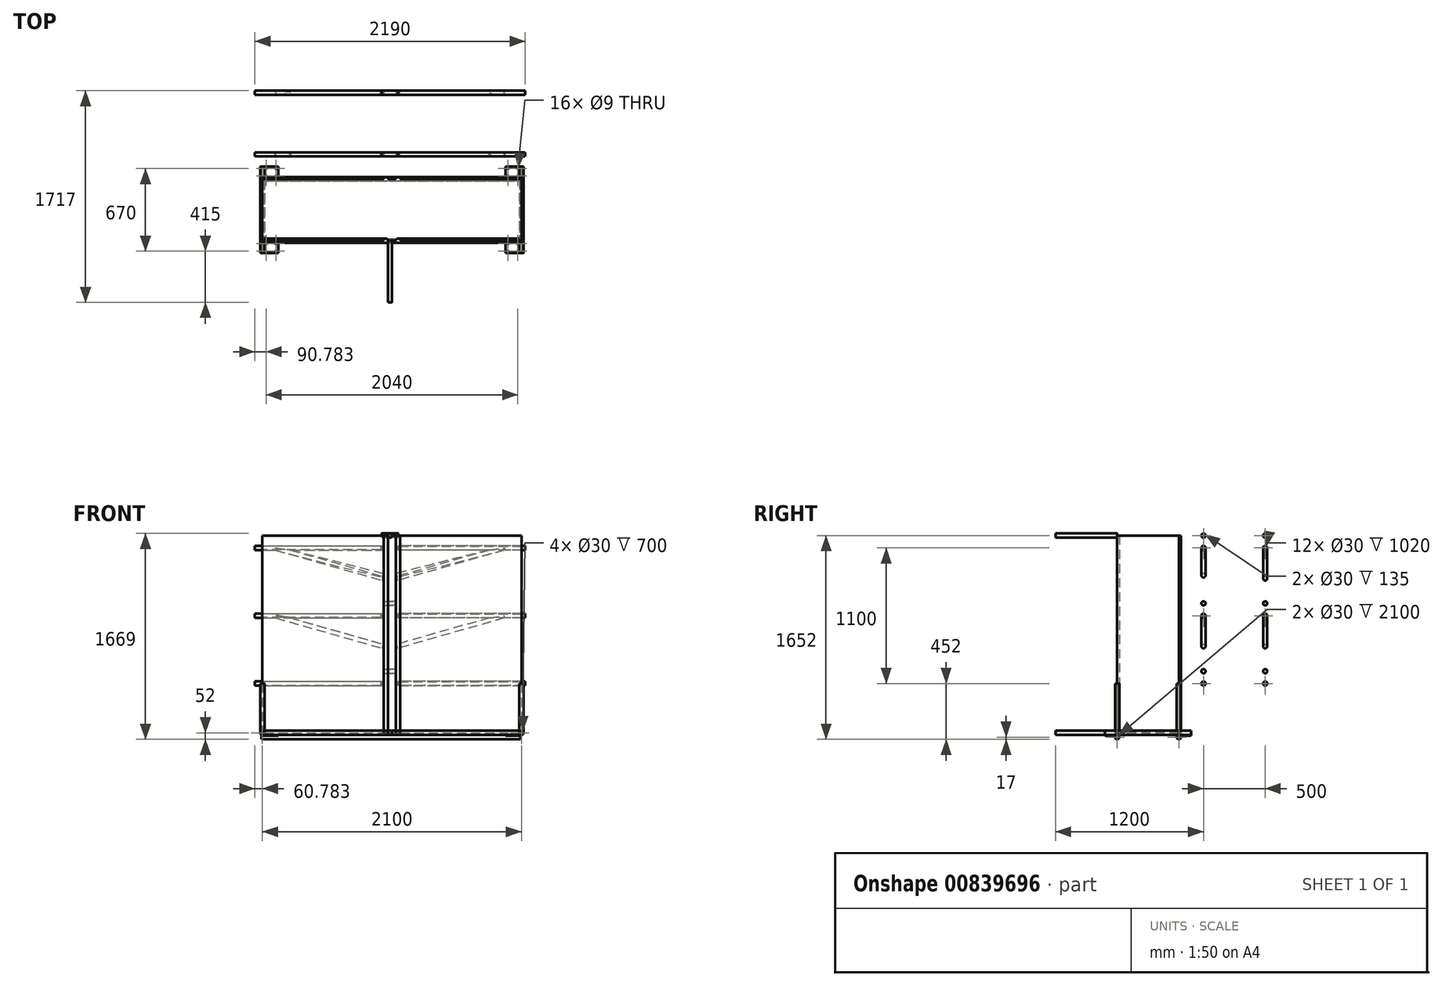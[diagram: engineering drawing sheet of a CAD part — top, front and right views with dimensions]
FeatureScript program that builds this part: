
annotation { "Feature Type Name" : "Feature", "Feature Type Description" : "" }
export const myFeature = defineFeature(function(context is Context, id is Id, definition is map)
    precondition{}
    {
        {
            var Q0;
            Q0=qCreatedBy(makeId("Top.planeOp"),FACE);
            var sketch = newSketch(context, id + "F0", { "sketchPlane" : qUnion([Q0])});
            skLineSegment(sketch, "E0.bottom", {"start": v(-1042.1, -100) * mm, "end": v(-59.1, -100) * mm});
            skLineSegment(sketch, "E0.top", {"start": v(-1042.1, -600) * mm, "end": v(-59.1, -600) * mm});
            skLineSegment(sketch, "E0.left", {"start": v(-1042.1, -100) * mm, "end": v(-1042.1, -600) * mm});
            skLineSegment(sketch, "E0.right", {"start": v(1057.9, -100) * mm, "end": v(1057.9, -600) * mm});
            skLineSegment(sketch, "E1", {"start": v(-1042.1, -100) * mm, "end": v(-1042.1, 0) * mm});
            skLineSegment(sketch, "E2", {"start": v(-1042.1, -600) * mm, "end": v(-1042.1, -700) * mm});
            skLineSegment(sketch, "E3", {"start": v(1057.9, -100) * mm, "end": v(1057.9, 0) * mm});
            skLineSegment(sketch, "E4", {"start": v(1057.9, -600) * mm, "end": v(1057.9, -700) * mm});
            skCircle(sketch, "E5", {"center": v(-42.1, -100) * mm, "radius": 17 * mm});
            skCircle(sketch, "E6", {"center": v(57.9, -100) * mm, "radius": 17 * mm});
            skLineSegment(sketch, "E7", {"start": v(1057.9, -350) * mm, "end": v(160.93, -350) * mm, "construction": true});
            skCircle(sketch, "E8.MirrorC", {"center": v(-42.1, -600) * mm, "radius": 17 * mm});
            skCircle(sketch, "E9.MirrorC", {"center": v(57.9, -600) * mm, "radius": 17 * mm});
            skLineSegment(sketch, "E10.trimOffspring", {"start": v(-25.1, -100) * mm, "end": v(40.9, -100) * mm});
            skLineSegment(sketch, "E11.trimOffspring", {"start": v(74.9, -100) * mm, "end": v(1057.9, -100) * mm});
            skLineSegment(sketch, "E12.trimOffspring", {"start": v(-25.1, -600) * mm, "end": v(40.9, -600) * mm});
            skLineSegment(sketch, "E13.trimOffspring", {"start": v(74.9, -600) * mm, "end": v(1057.9, -600) * mm});
            skSolve(sketch);
        }
        {
            var Q0;
            {var subQ0=sQuery(id+"F0.wireOp",EDGE,"E5");var subQ1=makeQuery(id+"F0.imprint","INTERSECT",VERTEX,{"derivedFrom":[sQuery(id+"F0.wireOp",EDGE,"E0.bottom"),subQ0]});Q0=makeQuery(id+"F0.imprint","IMPRINT",FACE,{"disambiguationData":[TD([[makeQuery(id+"F0.imprint","IMPRINT",EDGE,{"disambiguationData":[TD([[subQ1,1.0]])],"derivedFrom":subQ0}),1.0]])]});}
            var Q1;
            {var subQ0=sQuery(id+"F0.wireOp",EDGE,"E6");var subQ1=makeQuery(id+"F0.imprint","INTERSECT",VERTEX,{"derivedFrom":[subQ0,sQuery(id+"F0.wireOp",EDGE,"E10.trimOffspring")]});Q1=makeQuery(id+"F0.imprint","IMPRINT",FACE,{"disambiguationData":[TD([[makeQuery(id+"F0.imprint","IMPRINT",EDGE,{"disambiguationData":[TD([[subQ1,1.0]])],"derivedFrom":subQ0}),1.0]])]});}
            var Q2;
            {var subQ0=sQuery(id+"F0.wireOp",EDGE,"E8.MirrorC");var subQ1=makeQuery(id+"F0.imprint","INTERSECT",VERTEX,{"derivedFrom":[sQuery(id+"F0.wireOp",EDGE,"E0.top"),subQ0]});Q2=makeQuery(id+"F0.imprint","IMPRINT",FACE,{"disambiguationData":[TD([[makeQuery(id+"F0.imprint","IMPRINT",EDGE,{"disambiguationData":[TD([[subQ1,1.0]])],"derivedFrom":subQ0}),-1.0]])]});}
            var Q3;
            {var subQ0=sQuery(id+"F0.wireOp",EDGE,"E9.MirrorC");var subQ1=makeQuery(id+"F0.imprint","INTERSECT",VERTEX,{"derivedFrom":[subQ0,sQuery(id+"F0.wireOp",EDGE,"E12.trimOffspring")]});Q3=makeQuery(id+"F0.imprint","IMPRINT",FACE,{"disambiguationData":[TD([[makeQuery(id+"F0.imprint","IMPRINT",EDGE,{"disambiguationData":[TD([[subQ1,1.0]])],"derivedFrom":subQ0}),-1.0]])]});}
            extrude(context, id + "F1", {"entities" : qUnion([Q0, Q1, Q2, Q3]), "depth" : 1600 * mm, "offsetDistance" : 25 * mm});
        }
        {
            var Q0;
            Q0=sQuery(id+"F0.wireOp",EDGE,"E1");
            cPlane(context, id + "F2", {"entities" : qUnion([Q0]), "cplaneType" : CPlaneType.MID_PLANE, "offset" : 25 * mm, "width" : 150 * mm, "height" : 150 * mm});
        }
        {
            var Q0;
            Q0=qCreatedBy(id+"F2.planeOp",FACE);
            var sketch = newSketch(context, id + "F3", { "sketchPlane" : qUnion([Q0])});
            skCircle(sketch, "E14", {"center": v(1042.1, 0) * mm, "radius": 17 * mm});
            skCircle(sketch, "E15", {"center": v(-1057.9, 0) * mm, "radius": 17 * mm});
            skSolve(sketch);
        }
        {
            var Q0;
            Q0 = qSketchRegion(id + "F3", true);
            extrude(context, id + "F4", {"entities" : qUnion([Q0]), "depth" : 50 * mm, "offsetDistance" : 25 * mm, "hasSecondDirection" : true, "secondDirectionOppositeDirection" : true, "secondDirectionDepth" : 650 * mm});
        }
        {
            var Q0;
            Q0 = qSketchRegion(id + "F3", true);
            extrude(context, id + "F5", {"entities" : qUnion([Q0]), "depth" : 50 * mm, "offsetDistance" : 25 * mm, "hasSecondDirection" : true, "secondDirectionOppositeDirection" : true, "secondDirectionDepth" : 650 * mm});
        }
        {
            var Q0;
            Q0=sQuery(id+"F0.wireOp",EDGE,"E0.bottom");
            cPlane(context, id + "F6", {"entities" : qUnion([Q0]), "cplaneType" : CPlaneType.MID_PLANE, "offset" : 25 * mm, "width" : 150 * mm, "height" : 150 * mm});
        }
        {
            var Q0;
            Q0=qCreatedBy(id+"F6.planeOp",FACE);
            var sketch = newSketch(context, id + "F7", { "sketchPlane" : qUnion([Q0])});
            skCircle(sketch, "E16", {"center": v(-100, 0) * mm, "radius": 17 * mm});
            skCircle(sketch, "E17", {"center": v(-600, 0) * mm, "radius": 17 * mm});
            skSolve(sketch);
        }
        {
            var Q0;
            Q0 = qSketchRegion(id + "F7", true);
            extrude(context, id + "F8", {"entities" : qUnion([Q0]), "oppositeDirection" : true, "depth" : 500 * mm, "offsetDistance" : 25 * mm, "hasSecondDirection" : true, "secondDirectionOppositeDirection" : false, "secondDirectionDepth" : 1600 * mm});
        }
        {
            var Q0;
            Q0=qCreatedBy(makeId("Top.planeOp"),FACE);
            cPlane(context, id + "F9", {"entities" : qUnion([Q0]), "cplaneType" : CPlaneType.OFFSET, "offset" : 17.5 * mm, "oppositeDirection" : true, "width" : 150 * mm, "height" : 150 * mm});
        }
        {
            var Q0;
            Q0=qCreatedBy(id+"F9.planeOp",FACE);
            var sketch = newSketch(context, id + "F10", { "sketchPlane" : qUnion([Q0])});
            skLineSegment(sketch, "E18.bottom", {"start": v(-1042.1, -600) * mm, "end": v(-912.1, -600) * mm});
            skLineSegment(sketch, "E18.top", {"start": v(-1042.1, -700) * mm, "end": v(-912.1, -700) * mm});
            skLineSegment(sketch, "E18.left", {"start": v(-1042.1, -600) * mm, "end": v(-1042.1, -700) * mm});
            skLineSegment(sketch, "E18.right", {"start": v(-912.1, -600) * mm, "end": v(-912.1, -700) * mm});
            skCircle(sketch, "E19", {"center": v(-1012.1, -685) * mm, "radius": 4.5 * mm});
            skCircle(sketch, "E20", {"center": v(-932.1, -685) * mm, "radius": 4.5 * mm});
            skCircle(sketch, "E21", {"center": v(-1012.1, -625) * mm, "radius": 4.5 * mm});
            skCircle(sketch, "E22", {"center": v(-932.1, -625) * mm, "radius": 4.5 * mm});
            skLineSegment(sketch, "E23.bottom", {"start": v(-1007.6, -685) * mm, "end": v(-936.6, -685) * mm, "construction": true});
            skLineSegment(sketch, "E23.top", {"start": v(-1007.6, -625) * mm, "end": v(-936.6, -625) * mm, "construction": true});
            skLineSegment(sketch, "E23.left", {"start": v(-1012.1, -680.5) * mm, "end": v(-1012.1, -629.5) * mm, "construction": true});
            skLineSegment(sketch, "E23.right", {"start": v(-932.1, -680.5) * mm, "end": v(-932.1, -629.5) * mm, "construction": true});
            skLineSegment(sketch, "E24", {"start": v(-972.1, -685) * mm, "end": v(-972.1, -625) * mm, "construction": true});
            skLineSegment(sketch, "E25", {"start": v(-1012.1, -655) * mm, "end": v(-932.1, -655) * mm, "construction": true});
            skLineSegment(sketch, "E26", {"start": v(7.9, -600) * mm, "end": v(7.9, -303.37) * mm, "construction": true});
            skLineSegment(sketch, "E27", {"start": v(-1042.1, -350) * mm, "end": v(-775.86, -350) * mm, "construction": true});
            skLineSegment(sketch, "E28.MirrorCS", {"start": v(-1042.1, -100) * mm, "end": v(-912.1, -100) * mm});
            skLineSegment(sketch, "E29.MirrorCS", {"start": v(-912.1, -100) * mm, "end": v(-912.1, 0) * mm});
            skLineSegment(sketch, "E30.MirrorCS", {"start": v(-1042.1, 0) * mm, "end": v(-912.1, 0) * mm});
            skLineSegment(sketch, "E31.MirrorCS", {"start": v(-1042.1, -100) * mm, "end": v(-1042.1, 0) * mm});
            skCircle(sketch, "E32.MirrorC", {"center": v(-1012.1, -15) * mm, "radius": 4.5 * mm});
            skCircle(sketch, "E33.MirrorC", {"center": v(-932.1, -15) * mm, "radius": 4.5 * mm});
            skCircle(sketch, "E34.MirrorC", {"center": v(-932.1, -75) * mm, "radius": 4.5 * mm});
            skCircle(sketch, "E35.MirrorC", {"center": v(-1012.1, -75) * mm, "radius": 4.5 * mm});
            skLineSegment(sketch, "E36.MirrorCS", {"start": v(1057.9, -700) * mm, "end": v(927.9, -700) * mm});
            skLineSegment(sketch, "E37.MirrorCS", {"start": v(1057.9, -600) * mm, "end": v(1057.9, -700) * mm});
            skLineSegment(sketch, "E38.MirrorCS", {"start": v(927.9, -600) * mm, "end": v(927.9, -700) * mm});
            skLineSegment(sketch, "E39.MirrorCS", {"start": v(1057.9, -600) * mm, "end": v(927.9, -600) * mm});
            skCircle(sketch, "E40.MirrorC", {"center": v(947.9, -625) * mm, "radius": 4.5 * mm});
            skCircle(sketch, "E41.MirrorC", {"center": v(947.9, -685) * mm, "radius": 4.5 * mm});
            skCircle(sketch, "E42.MirrorC", {"center": v(1027.9, -685) * mm, "radius": 4.5 * mm});
            skCircle(sketch, "E43.MirrorC", {"center": v(1027.9, -625) * mm, "radius": 4.5 * mm});
            skLineSegment(sketch, "E44.MirrorCS", {"start": v(1057.9, -100) * mm, "end": v(927.9, -100) * mm});
            skLineSegment(sketch, "E45.MirrorCS", {"start": v(927.9, -100) * mm, "end": v(927.9, 0) * mm});
            skLineSegment(sketch, "E46.MirrorCS", {"start": v(1057.9, -100) * mm, "end": v(1057.9, 0) * mm});
            skLineSegment(sketch, "E47.MirrorCS", {"start": v(1057.9, 0) * mm, "end": v(927.9, 0) * mm});
            skCircle(sketch, "E48.MirrorC", {"center": v(947.9, -15) * mm, "radius": 4.5 * mm});
            skCircle(sketch, "E49.MirrorC", {"center": v(947.9, -75) * mm, "radius": 4.5 * mm});
            skCircle(sketch, "E50.MirrorC", {"center": v(1027.9, -75) * mm, "radius": 4.5 * mm});
            skCircle(sketch, "E51.MirrorC", {"center": v(1027.9, -15) * mm, "radius": 4.5 * mm});
            skLineSegment(sketch, "E52", {"start": v(-972.1, -700) * mm, "end": v(-972.1, -600) * mm, "construction": true});
            skLineSegment(sketch, "E53", {"start": v(-1042.1, -655) * mm, "end": v(-912.1, -655) * mm, "construction": true});
            skSolve(sketch);
        }
        {
            var Q0;
            Q0 = qSketchRegion(id + "F10", true);
            extrude(context, id + "F11", {"entities" : qUnion([Q0]), "oppositeDirection" : true, "depth" : 4 * mm, "offsetDistance" : 25 * mm});
        }
        {
            var Q0;
            Q0=qCreatedBy(id+"F9.planeOp",FACE);
            cPlane(context, id + "F12", {"entities" : qUnion([Q0]), "cplaneType" : CPlaneType.OFFSET, "offset" : 17.5 * mm, "oppositeDirection" : true, "width" : 150 * mm, "height" : 150 * mm});
        }
        {
            var Q0;
            Q0=qCreatedBy(id+"F12.planeOp",FACE);
            var sketch = newSketch(context, id + "F13", { "sketchPlane" : qUnion([Q0])});
            skLineSegment(sketch, "E54", {"start": v(-1042.1, -600) * mm, "end": v(1057.9, -600) * mm});
            skLineSegment(sketch, "E55", {"start": v(-1042.1, -100) * mm, "end": v(1057.9, -100) * mm});
            skSolve(sketch);
        }
        {
            var Q0;
            Q0=qCreatedBy(id+"F6.planeOp",FACE);
            var sketch = newSketch(context, id + "F14", { "sketchPlane" : qUnion([Q0])});
            skCircle(sketch, "E56", {"center": v(-100, -35) * mm, "radius": 17 * mm});
            skCircle(sketch, "E57", {"center": v(-600, -35) * mm, "radius": 17 * mm});
            skSolve(sketch);
        }
        {
            var Q0;
            Q0 = qSketchRegion(id + "F14", true);
            extrude(context, id + "F15", {"entities" : qUnion([Q0]), "oppositeDirection" : true, "depth" : 500 * mm, "offsetDistance" : 25 * mm, "hasSecondDirection" : true, "secondDirectionOppositeDirection" : false, "secondDirectionDepth" : 1600 * mm});
        }
        {
            var Q0;
            Q0=makeQuery(id+"F1.opExtrude","SWEPT_FACE",FACE,{"disambiguationData":[OSD([sQuery(id+"F0.wireOp",EDGE,"E9.MirrorC")])]});
            var Q1;
            Q1=makeQuery(id+"F1.opExtrude","SWEPT_FACE",FACE,{"disambiguationData":[OSD([sQuery(id+"F0.wireOp",EDGE,"E8.MirrorC")])]});
            cPlane(context, id + "F16", {"entities" : qUnion([Q0, Q1]), "cplaneType" : CPlaneType.LINE_ANGLE, "offset" : 25 * mm, "angle" : 0 * degree, "width" : 150 * mm, "height" : 150 * mm});
        }
        {
            var Q0;
            Q0=qCreatedBy(id+"F16.planeOp",FACE);
            var sketch = newSketch(context, id + "F17", { "sketchPlane" : qUnion([Q0])});
            skCircle(sketch, "E58", {"center": v(-7.9, 0) * mm, "radius": 17 * mm});
            skSolve(sketch);
        }
        {
            var Q0;
            Q0 = qSketchRegion(id + "F17", true);
            extrude(context, id + "F18", {"entities" : qUnion([Q0]), "depth" : 500 * mm, "offsetDistance" : 25 * mm});
        }
        {
            var Q0;
            Q0=qCreatedBy(id+"F16.planeOp",FACE);
            var sketch = newSketch(context, id + "F19", { "sketchPlane" : qUnion([Q0])});
            skLineSegment(sketch, "E59", {"start": v(-57.9, 0) * mm, "end": v(-57.9, 1600) * mm});
            skLineSegment(sketch, "E60", {"start": v(42.1, 0) * mm, "end": v(42.1, 1600) * mm});
            skLineSegment(sketch, "E61", {"start": v(42.1, 500) * mm, "end": v(-57.9, 500) * mm});
            skLineSegment(sketch, "E62", {"start": v(42.1, 1050) * mm, "end": v(-57.9, 1050) * mm});
            skLineSegment(sketch, "E63", {"start": v(-57.9, 400) * mm, "end": v(-1087.9, 400) * mm});
            skLineSegment(sketch, "E64", {"start": v(42.1, 400) * mm, "end": v(1072.1, 400) * mm});
            skLineSegment(sketch, "E65", {"start": v(-57.9, 950) * mm, "end": v(-1087.9, 950) * mm});
            skLineSegment(sketch, "E66", {"start": v(42.1, 950) * mm, "end": v(1072.1, 950) * mm});
            skLineSegment(sketch, "E67", {"start": v(-57.9, 1500) * mm, "end": v(-1087.9, 1500) * mm});
            skLineSegment(sketch, "E68", {"start": v(42.1, 1500) * mm, "end": v(1072.1, 1500) * mm});
            skLineSegment(sketch, "E69", {"start": v(42.1, 1600) * mm, "end": v(-57.9, 1600) * mm});
            skLineSegment(sketch, "E70", {"start": v(-1057.9, 400) * mm, "end": v(-1057.9, 0) * mm});
            skLineSegment(sketch, "E71", {"start": v(1042.1, 400) * mm, "end": v(1042.1, 0) * mm});
            skLineSegment(sketch, "E72", {"start": v(-57.9, 700) * mm, "end": v(-937.9, 950) * mm});
            skLineSegment(sketch, "E73", {"start": v(42.1, 700) * mm, "end": v(922.1, 950) * mm});
            skLineSegment(sketch, "E74", {"start": v(-57.9, 1250) * mm, "end": v(-937.9, 1500) * mm});
            skLineSegment(sketch, "E75", {"start": v(42.1, 1250) * mm, "end": v(922.1, 1500) * mm});
            skSolve(sketch);
        }
        {
            var Q0;
            Q0=sQuery(id+"F19.wireOp",EDGE,"E67");
            cPlane(context, id + "F20", {"entities" : qUnion([Q0]), "cplaneType" : CPlaneType.MID_PLANE, "offset" : 25 * mm, "width" : 150 * mm, "height" : 150 * mm});
        }
        {
            var Q0;
            Q0=qCreatedBy(id+"F20.planeOp",FACE);
            var sketch = newSketch(context, id + "F21", { "sketchPlane" : qUnion([Q0])});
            skCircle(sketch, "E76", {"center": v(-600, 1500) * mm, "radius": 17 * mm});
            skCircle(sketch, "E77", {"center": v(-600, 950) * mm, "radius": 17 * mm});
            skCircle(sketch, "E78", {"center": v(-600, 400) * mm, "radius": 17 * mm});
            skSolve(sketch);
        }
        {
            var Q0;
            Q0 = qSketchRegion(id + "F21", true);
            extrude(context, id + "F22", {"entities" : qUnion([Q0]), "operationType" : NewBodyOperationType.ADD, "depth" : 530 * mm, "offsetDistance" : 25 * mm, "hasSecondDirection" : true, "secondDirectionOppositeDirection" : true, "secondDirectionDepth" : 500 * mm});
        }
        {
            var Q0;
            Q0=sQuery(id+"F19.wireOp",EDGE,"E68");
            cPlane(context, id + "F23", {"entities" : qUnion([Q0]), "cplaneType" : CPlaneType.MID_PLANE, "offset" : 25 * mm, "width" : 150 * mm, "height" : 150 * mm});
        }
        {
            var Q0;
            Q0=qCreatedBy(id+"F23.planeOp",FACE);
            var sketch = newSketch(context, id + "F24", { "sketchPlane" : qUnion([Q0])});
            skCircle(sketch, "E79", {"center": v(600, 1500) * mm, "radius": 17 * mm});
            skCircle(sketch, "E80", {"center": v(600, 950) * mm, "radius": 17 * mm});
            skCircle(sketch, "E81", {"center": v(600, 400) * mm, "radius": 17 * mm});
            skSolve(sketch);
        }
        {
            var Q0;
            Q0 = qSketchRegion(id + "F24", true);
            extrude(context, id + "F25", {"entities" : qUnion([Q0]), "operationType" : NewBodyOperationType.ADD, "depth" : 530 * mm, "offsetDistance" : 25 * mm, "hasSecondDirection" : true, "secondDirectionOppositeDirection" : true, "secondDirectionDepth" : 500 * mm});
        }
        {
            var Q0;
            Q0=sQuery(id+"F19.wireOp",EDGE,"E74");
            cPlane(context, id + "F26", {"entities" : qUnion([Q0]), "cplaneType" : CPlaneType.MID_PLANE, "offset" : 25 * mm, "width" : 150 * mm, "height" : 150 * mm});
        }
        {
            var Q0;
            Q0=qCreatedBy(id+"F26.planeOp",FACE);
            var sketch = newSketch(context, id + "F27", { "sketchPlane" : qUnion([Q0])});
            skCircle(sketch, "E82", {"center": v(-600, 1186.6) * mm, "radius": 17 * mm});
            skSolve(sketch);
        }
        {
            var Q0;
            Q0 = qSketchRegion(id + "F27", true);
            extrude(context, id + "F28", {"entities" : qUnion([Q0]), "operationType" : NewBodyOperationType.ADD, "depth" : 450 * mm, "offsetDistance" : 25 * mm, "hasSecondDirection" : true, "secondDirectionOppositeDirection" : true, "secondDirectionDepth" : 450 * mm});
        }
        {
            var Q0;
            Q0=sQuery(id+"F19.wireOp",EDGE,"E75");
            cPlane(context, id + "F29", {"entities" : qUnion([Q0]), "cplaneType" : CPlaneType.MID_PLANE, "offset" : 25 * mm, "width" : 150 * mm, "height" : 150 * mm});
        }
        {
            var Q0;
            Q0=qCreatedBy(id+"F29.planeOp",FACE);
            var sketch = newSketch(context, id + "F30", { "sketchPlane" : qUnion([Q0])});
            skCircle(sketch, "E83", {"center": v(600, 1190.91) * mm, "radius": 17 * mm});
            skSolve(sketch);
        }
        {
            var Q0;
            Q0 = qSketchRegion(id + "F30", true);
            extrude(context, id + "F31", {"entities" : qUnion([Q0]), "operationType" : NewBodyOperationType.ADD, "depth" : 450 * mm, "offsetDistance" : 25 * mm, "hasSecondDirection" : true, "secondDirectionOppositeDirection" : true, "secondDirectionDepth" : 450 * mm});
        }
        {
            var Q0;
            Q0=sQuery(id+"F19.wireOp",EDGE,"E69");
            cPlane(context, id + "F32", {"entities" : qUnion([Q0]), "cplaneType" : CPlaneType.MID_PLANE, "offset" : 25 * mm, "width" : 150 * mm, "height" : 150 * mm});
        }
        {
            var Q0;
            Q0=qCreatedBy(id+"F32.planeOp",FACE);
            var sketch = newSketch(context, id + "F33", { "sketchPlane" : qUnion([Q0])});
            skCircle(sketch, "E84", {"center": v(-600, 1600) * mm, "radius": 17 * mm});
            skCircle(sketch, "E85", {"center": v(-600, 1050) * mm, "radius": 17 * mm});
            skCircle(sketch, "E86", {"center": v(-600, 500) * mm, "radius": 17 * mm});
            skSolve(sketch);
        }
        {
            var Q0;
            Q0=makeQuery(id+"F33.imprint","IMPRINT",FACE,{"disambiguationData":[TD([[makeQuery(id+"F33.imprint","IMPRINT",EDGE,{"derivedFrom":sQuery(id+"F33.wireOp",EDGE,"E85")}),1.0]])]});
            var Q1;
            Q1=makeQuery(id+"F33.imprint","IMPRINT",FACE,{"disambiguationData":[TD([[makeQuery(id+"F33.imprint","IMPRINT",EDGE,{"derivedFrom":sQuery(id+"F33.wireOp",EDGE,"E86")}),1.0]])]});
            extrude(context, id + "F34", {"entities" : qUnion([Q0, Q1]), "depth" : 50 * mm, "offsetDistance" : 25 * mm, "hasSecondDirection" : true, "secondDirectionOppositeDirection" : true, "secondDirectionDepth" : 50 * mm});
        }
        {
            var Q0;
            Q0=makeQuery(id+"F33.imprint","IMPRINT",FACE,{"disambiguationData":[TD([[makeQuery(id+"F33.imprint","IMPRINT",EDGE,{"derivedFrom":sQuery(id+"F33.wireOp",EDGE,"E84")}),1.0]])]});
            extrude(context, id + "F35", {"entities" : qUnion([Q0]), "depth" : 67.5 * mm, "offsetDistance" : 25 * mm, "hasSecondDirection" : true, "secondDirectionOppositeDirection" : true, "secondDirectionDepth" : 67.5 * mm});
        }
        {
            var Q0;
            Q0=sQuery(id+"F19.wireOp",EDGE,"E72");
            cPlane(context, id + "F36", {"entities" : qUnion([Q0]), "cplaneType" : CPlaneType.MID_PLANE, "offset" : 25 * mm, "width" : 150 * mm, "height" : 150 * mm});
        }
        {
            var Q0;
            Q0=qCreatedBy(id+"F36.planeOp",FACE);
            var sketch = newSketch(context, id + "F37", { "sketchPlane" : qUnion([Q0])});
            skCircle(sketch, "E87", {"center": v(-600, 657.53) * mm, "radius": 17 * mm});
            skSolve(sketch);
        }
        {
            var Q0;
            Q0 = qSketchRegion(id + "F37", true);
            extrude(context, id + "F38", {"entities" : qUnion([Q0]), "depth" : 450 * mm, "offsetDistance" : 25 * mm, "hasSecondDirection" : true, "secondDirectionOppositeDirection" : true, "secondDirectionDepth" : 450 * mm});
        }
        {
            var Q0;
            Q0=sQuery(id+"F19.wireOp",EDGE,"E73");
            cPlane(context, id + "F39", {"entities" : qUnion([Q0]), "cplaneType" : CPlaneType.MID_PLANE, "offset" : 25 * mm, "width" : 150 * mm, "height" : 150 * mm});
        }
        {
            var Q0;
            Q0=qCreatedBy(id+"F39.planeOp",FACE);
            var sketch = newSketch(context, id + "F40", { "sketchPlane" : qUnion([Q0])});
            skCircle(sketch, "E88", {"center": v(600, 661.85) * mm, "radius": 17 * mm});
            skSolve(sketch);
        }
        {
            var Q0;
            Q0 = qSketchRegion(id + "F40", true);
            extrude(context, id + "F41", {"entities" : qUnion([Q0]), "operationType" : NewBodyOperationType.ADD, "depth" : 450 * mm, "offsetDistance" : 25 * mm, "hasSecondDirection" : true, "secondDirectionOppositeDirection" : true, "secondDirectionDepth" : 450 * mm});
        }
        {
            var Q0;
            Q0=qCreatedBy(id+"F16.planeOp",FACE);
            cPlane(context, id + "F42", {"entities" : qUnion([Q0]), "cplaneType" : CPlaneType.OFFSET, "offset" : 500 * mm, "width" : 150 * mm, "height" : 150 * mm});
        }
        {
            var Q0;
            Q0=qCreatedBy(id+"F42.planeOp",FACE);
            var sketch = newSketch(context, id + "F43", { "sketchPlane" : qUnion([Q0])});
            skLineSegment(sketch, "E89", {"start": v(42.1, 0) * mm, "end": v(42.1, 1600) * mm});
            skLineSegment(sketch, "E90", {"start": v(-57.9, 0) * mm, "end": v(-57.9, 1600) * mm});
            skLineSegment(sketch, "E91", {"start": v(-57.9, 500) * mm, "end": v(42.1, 500) * mm});
            skLineSegment(sketch, "E92", {"start": v(-57.9, 1050) * mm, "end": v(42.1, 1050) * mm});
            skLineSegment(sketch, "E93", {"start": v(-57.9, 1600) * mm, "end": v(42.1, 1600) * mm});
            skLineSegment(sketch, "E94", {"start": v(42.1, 400) * mm, "end": v(1072.1, 400) * mm});
            skLineSegment(sketch, "E95", {"start": v(-57.9, 400) * mm, "end": v(-1087.9, 400) * mm});
            skLineSegment(sketch, "E96", {"start": v(42.1, 950) * mm, "end": v(1072.1, 950) * mm});
            skLineSegment(sketch, "E97", {"start": v(-57.9, 950) * mm, "end": v(-1087.9, 950) * mm});
            skLineSegment(sketch, "E98", {"start": v(42.1, 1500) * mm, "end": v(1072.1, 1500) * mm});
            skLineSegment(sketch, "E99", {"start": v(-57.9, 1500) * mm, "end": v(-1087.9, 1500) * mm});
            skLineSegment(sketch, "E100", {"start": v(1042.1, 400) * mm, "end": v(1042.1, 0) * mm});
            skLineSegment(sketch, "E101", {"start": v(-1057.9, 400) * mm, "end": v(-1057.9, 0) * mm});
            skLineSegment(sketch, "E102", {"start": v(42.1, 700) * mm, "end": v(922.1, 950) * mm});
            skLineSegment(sketch, "E103", {"start": v(42.1, 1274.83) * mm, "end": v(928.79, 1500) * mm});
            skLineSegment(sketch, "E104", {"start": v(-57.9, 1274.83) * mm, "end": v(-944.57, 1500) * mm});
            skLineSegment(sketch, "E105", {"start": v(-57.9, 700) * mm, "end": v(-937.9, 950) * mm});
            skSolve(sketch);
        }
        {
            var Q0;
            Q0=sQuery(id+"F43.wireOp",EDGE,"E98");
            cPlane(context, id + "F44", {"entities" : qUnion([Q0]), "cplaneType" : CPlaneType.MID_PLANE, "offset" : 25 * mm, "width" : 150 * mm, "height" : 150 * mm});
        }
        {
            var Q0;
            Q0=qCreatedBy(id+"F44.planeOp",FACE);
            var sketch = newSketch(context, id + "F45", { "sketchPlane" : qUnion([Q0])});
            skCircle(sketch, "E106", {"center": v(100, 1500) * mm, "radius": 17 * mm});
            skCircle(sketch, "E107", {"center": v(100, 950) * mm, "radius": 17 * mm});
            skCircle(sketch, "E108", {"center": v(100, 400) * mm, "radius": 17 * mm});
            skSolve(sketch);
        }
        {
            var Q0;
            Q0 = qSketchRegion(id + "F45", true);
            extrude(context, id + "F46", {"entities" : qUnion([Q0]), "operationType" : NewBodyOperationType.ADD, "depth" : 530 * mm, "offsetDistance" : 25 * mm, "hasSecondDirection" : true, "secondDirectionOppositeDirection" : true, "secondDirectionDepth" : 500 * mm});
        }
        {
            var Q0;
            Q0=sQuery(id+"F43.wireOp",EDGE,"E99");
            cPlane(context, id + "F47", {"entities" : qUnion([Q0]), "cplaneType" : CPlaneType.MID_PLANE, "offset" : 25 * mm, "width" : 150 * mm, "height" : 150 * mm});
        }
        {
            var Q0;
            Q0=qCreatedBy(id+"F47.planeOp",FACE);
            var sketch = newSketch(context, id + "F48", { "sketchPlane" : qUnion([Q0])});
            skCircle(sketch, "E109", {"center": v(-100, 1500) * mm, "radius": 17 * mm});
            skCircle(sketch, "E110", {"center": v(-100, 950) * mm, "radius": 17 * mm});
            skCircle(sketch, "E111", {"center": v(-100, 400) * mm, "radius": 17 * mm});
            skSolve(sketch);
        }
        {
            var Q0;
            Q0 = qSketchRegion(id + "F48", true);
            extrude(context, id + "F49", {"entities" : qUnion([Q0]), "operationType" : NewBodyOperationType.ADD, "depth" : 530 * mm, "offsetDistance" : 25 * mm, "hasSecondDirection" : true, "secondDirectionOppositeDirection" : true, "secondDirectionDepth" : 500 * mm});
        }
        {
            var Q0;
            Q0=sQuery(id+"F43.wireOp",EDGE,"E102");
            cPlane(context, id + "F50", {"entities" : qUnion([Q0]), "cplaneType" : CPlaneType.MID_PLANE, "offset" : 25 * mm, "width" : 150 * mm, "height" : 150 * mm});
        }
        {
            var Q0;
            Q0=qCreatedBy(id+"F50.planeOp",FACE);
            var sketch = newSketch(context, id + "F51", { "sketchPlane" : qUnion([Q0])});
            skCircle(sketch, "E112", {"center": v(100, 661.85) * mm, "radius": 17 * mm});
            skSolve(sketch);
        }
        {
            var Q0;
            Q0 = qSketchRegion(id + "F51", true);
            extrude(context, id + "F52", {"entities" : qUnion([Q0]), "operationType" : NewBodyOperationType.ADD, "depth" : 450 * mm, "offsetDistance" : 25 * mm, "hasSecondDirection" : true, "secondDirectionOppositeDirection" : true, "secondDirectionDepth" : 450 * mm});
        }
        {
            var Q0;
            Q0=sQuery(id+"F43.wireOp",EDGE,"E105");
            cPlane(context, id + "F53", {"entities" : qUnion([Q0]), "cplaneType" : CPlaneType.MID_PLANE, "offset" : 25 * mm, "width" : 150 * mm, "height" : 150 * mm});
        }
        {
            var Q0;
            Q0=qCreatedBy(id+"F53.planeOp",FACE);
            var sketch = newSketch(context, id + "F54", { "sketchPlane" : qUnion([Q0])});
            skCircle(sketch, "E113", {"center": v(-100, 657.53) * mm, "radius": 17 * mm});
            skSolve(sketch);
        }
        {
            var Q0;
            Q0 = qSketchRegion(id + "F54", true);
            extrude(context, id + "F55", {"entities" : qUnion([Q0]), "operationType" : NewBodyOperationType.ADD, "depth" : 450 * mm, "offsetDistance" : 25 * mm, "hasSecondDirection" : true, "secondDirectionOppositeDirection" : true, "secondDirectionDepth" : 450 * mm});
        }
        {
            var Q0;
            Q0=sQuery(id+"F43.wireOp",EDGE,"E92");
            cPlane(context, id + "F56", {"entities" : qUnion([Q0]), "cplaneType" : CPlaneType.MID_PLANE, "offset" : 25 * mm, "width" : 150 * mm, "height" : 150 * mm});
        }
        {
            var Q0;
            Q0=qCreatedBy(id+"F56.planeOp",FACE);
            var sketch = newSketch(context, id + "F57", { "sketchPlane" : qUnion([Q0])});
            skCircle(sketch, "E114", {"center": v(100, 1050) * mm, "radius": 17 * mm});
            skCircle(sketch, "E115", {"center": v(100, 500) * mm, "radius": 17 * mm});
            skCircle(sketch, "E116", {"center": v(100, 1600) * mm, "radius": 17 * mm});
            skSolve(sketch);
        }
        {
            var Q0;
            Q0=makeQuery(id+"F57.imprint","IMPRINT",FACE,{"disambiguationData":[TD([[makeQuery(id+"F57.imprint","IMPRINT",EDGE,{"derivedFrom":sQuery(id+"F57.wireOp",EDGE,"E114")}),1.0]])]});
            var Q1;
            Q1=makeQuery(id+"F57.imprint","IMPRINT",FACE,{"disambiguationData":[TD([[makeQuery(id+"F57.imprint","IMPRINT",EDGE,{"derivedFrom":sQuery(id+"F57.wireOp",EDGE,"E115")}),1.0]])]});
            extrude(context, id + "F58", {"entities" : qUnion([Q0, Q1]), "operationType" : NewBodyOperationType.ADD, "depth" : 50 * mm, "offsetDistance" : 25 * mm, "hasSecondDirection" : true, "secondDirectionOppositeDirection" : true, "secondDirectionDepth" : 50 * mm});
        }
        {
            var Q0;
            Q0=makeQuery(id+"F57.imprint","IMPRINT",FACE,{"disambiguationData":[TD([[makeQuery(id+"F57.imprint","IMPRINT",EDGE,{"derivedFrom":sQuery(id+"F57.wireOp",EDGE,"E116")}),1.0]])]});
            extrude(context, id + "F59", {"entities" : qUnion([Q0]), "depth" : 67.5 * mm, "offsetDistance" : 25 * mm, "hasSecondDirection" : true, "secondDirectionOppositeDirection" : true, "secondDirectionDepth" : 67.5 * mm});
        }
        {
            var Q0;
            Q0=sQuery(id+"F43.wireOp",EDGE,"E103");
            cPlane(context, id + "F60", {"entities" : qUnion([Q0]), "cplaneType" : CPlaneType.MID_PLANE, "offset" : 25 * mm, "width" : 150 * mm, "height" : 150 * mm});
        }
        {
            var Q0;
            Q0=qCreatedBy(id+"F60.planeOp",FACE);
            var sketch = newSketch(context, id + "F61", { "sketchPlane" : qUnion([Q0])});
            skCircle(sketch, "E117", {"center": v(100, 1225.25) * mm, "radius": 17 * mm});
            skSolve(sketch);
        }
        {
            var Q0;
            Q0 = qSketchRegion(id + "F61", true);
            extrude(context, id + "F62", {"entities" : qUnion([Q0]), "operationType" : NewBodyOperationType.ADD, "depth" : 450 * mm, "offsetDistance" : 25 * mm, "hasSecondDirection" : true, "secondDirectionOppositeDirection" : true, "secondDirectionDepth" : 450 * mm});
        }
        {
            var Q0;
            Q0=sQuery(id+"F43.wireOp",EDGE,"E104");
            cPlane(context, id + "F63", {"entities" : qUnion([Q0]), "cplaneType" : CPlaneType.MID_PLANE, "offset" : 25 * mm, "width" : 150 * mm, "height" : 150 * mm});
        }
        {
            var Q0;
            Q0=qCreatedBy(id+"F63.planeOp",FACE);
            var sketch = newSketch(context, id + "F64", { "sketchPlane" : qUnion([Q0])});
            skCircle(sketch, "E118", {"center": v(-100, 1221.36) * mm, "radius": 17 * mm});
            skSolve(sketch);
        }
        {
            var Q0;
            Q0 = qSketchRegion(id + "F64", true);
            extrude(context, id + "F65", {"entities" : qUnion([Q0]), "operationType" : NewBodyOperationType.ADD, "depth" : 450 * mm, "offsetDistance" : 25 * mm, "hasSecondDirection" : true, "secondDirectionOppositeDirection" : true, "secondDirectionDepth" : 450 * mm});
        }
        {
            var Q0;
            Q0=sQuery(id+"F19.wireOp",EDGE,"E71");
            cPlane(context, id + "F66", {"entities" : qUnion([Q0]), "cplaneType" : CPlaneType.MID_PLANE, "offset" : 25 * mm, "width" : 150 * mm, "height" : 150 * mm});
        }
        {
            var Q0;
            Q0=qCreatedBy(id+"F66.planeOp",FACE);
            var sketch = newSketch(context, id + "F67", { "sketchPlane" : qUnion([Q0])});
            skCircle(sketch, "E119", {"center": v(-1042.1, 600) * mm, "radius": 17 * mm});
            skCircle(sketch, "E120", {"center": v(-1042.1, 100) * mm, "radius": 17 * mm});
            skCircle(sketch, "E121", {"center": v(1057.9, 600) * mm, "radius": 17.5 * mm});
            skCircle(sketch, "E122", {"center": v(1057.9, 100) * mm, "radius": 17.5 * mm});
            skSolve(sketch);
        }
        {
            var Q0;
            Q0 = qSketchRegion(id + "F67", true);
            extrude(context, id + "F68", {"entities" : qUnion([Q0]), "depth" : 200 * mm, "offsetDistance" : 25 * mm, "hasSecondDirection" : true, "secondDirectionOppositeDirection" : true, "secondDirectionDepth" : 200 * mm});
        }
        {
            var Q0;
            Q0=sQuery(id+"F19.wireOp",EDGE,"E69");
            var Q1;
            Q1=sQuery(id+"F19.wireOp",EDGE,"E60");
            cPlane(context, id + "F69", {"entities" : qUnion([Q0, Q1]), "cplaneType" : CPlaneType.LINE_ANGLE, "offset" : 25 * mm, "angle" : 0 * degree, "width" : 150 * mm, "height" : 150 * mm});
        }
        {
            var Q0;
            Q0=qCreatedBy(id+"F69.planeOp",FACE);
            var sketch = newSketch(context, id + "F70", { "sketchPlane" : qUnion([Q0])});
            skCircle(sketch, "E123", {"center": v(7.9, 1600) * mm, "radius": 17 * mm});
            skSolve(sketch);
        }
        {
            var Q0;
            Q0 = qSketchRegion(id + "F70", true);
            extrude(context, id + "F71", {"entities" : qUnion([Q0]), "oppositeDirection" : true, "depth" : 500 * mm, "offsetDistance" : 25 * mm});
        }
        {
            var Q0;
            Q0=makeQuery(id+"F22.opExtrude","CAP_FACE",FACE,{"disambiguationData":[OSD([sQuery(id+"F21.wireOp",EDGE,"E78")])],"isStart":false});
            var sketch = newSketch(context, id + "F72", { "sketchPlane" : qUnion([Q0])});
            skCircle(sketch, "E124", {"center": v(-600, 400) * mm, "radius": 15 * mm});
            skSolve(sketch);
        }
        {
            var Q0;
            Q0 = qSketchRegion(id + "F72", true);
            extrude(context, id + "F73", {"entities" : qUnion([Q0]), "operationType" : NewBodyOperationType.REMOVE, "oppositeDirection" : true, "depth" : 1020 * mm, "offsetDistance" : 25 * mm});
        }
        {
            var Q0;
            Q0=makeQuery(id+"F49.opExtrude","CAP_FACE",FACE,{"disambiguationData":[OSD([sQuery(id+"F48.wireOp",EDGE,"E111")])],"isStart":false});
            var sketch = newSketch(context, id + "F74", { "sketchPlane" : qUnion([Q0])});
            skCircle(sketch, "E125", {"center": v(-100, 400) * mm, "radius": 15 * mm});
            skSolve(sketch);
        }
        {
            var Q0;
            Q0 = qSketchRegion(id + "F74", true);
            extrude(context, id + "F75", {"entities" : qUnion([Q0]), "operationType" : NewBodyOperationType.REMOVE, "oppositeDirection" : true, "depth" : 1020 * mm, "offsetDistance" : 25 * mm});
        }
        {
            var Q0;
            Q0=makeQuery(id+"F49.opExtrude","CAP_FACE",FACE,{"disambiguationData":[OSD([sQuery(id+"F48.wireOp",EDGE,"E110")])],"isStart":false});
            var sketch = newSketch(context, id + "F76", { "sketchPlane" : qUnion([Q0])});
            skCircle(sketch, "E126", {"center": v(-100, 950) * mm, "radius": 15 * mm});
            skSolve(sketch);
        }
        {
            var Q0;
            Q0 = qSketchRegion(id + "F76", true);
            extrude(context, id + "F77", {"entities" : qUnion([Q0]), "operationType" : NewBodyOperationType.REMOVE, "oppositeDirection" : true, "depth" : 1020 * mm, "offsetDistance" : 25 * mm});
        }
        {
            var Q0;
            Q0=makeQuery(id+"F22.opExtrude","CAP_FACE",FACE,{"disambiguationData":[OSD([sQuery(id+"F21.wireOp",EDGE,"E77")])],"isStart":false});
            var sketch = newSketch(context, id + "F78", { "sketchPlane" : qUnion([Q0])});
            skCircle(sketch, "E127", {"center": v(-600, 950) * mm, "radius": 15 * mm});
            skSolve(sketch);
        }
        {
            var Q0;
            Q0=makeQuery(id+"F78.imprint","IMPRINT",FACE,{"disambiguationData":[TD([[makeQuery(id+"F78.imprint","IMPRINT",EDGE,{"derivedFrom":sQuery(id+"F78.wireOp",EDGE,"E127")}),1.0]])]});
            extrude(context, id + "F79", {"entities" : qUnion([Q0]), "operationType" : NewBodyOperationType.REMOVE, "oppositeDirection" : true, "depth" : 1020 * mm, "offsetDistance" : 25 * mm});
        }
        {
            var Q0;
            Q0=makeQuery(id+"F22.opExtrude","CAP_FACE",FACE,{"disambiguationData":[OSD([sQuery(id+"F21.wireOp",EDGE,"E76")])],"isStart":false});
            var sketch = newSketch(context, id + "F80", { "sketchPlane" : qUnion([Q0])});
            skCircle(sketch, "E128", {"center": v(-600, 1500) * mm, "radius": 15 * mm});
            skSolve(sketch);
        }
        {
            var Q0;
            Q0 = qSketchRegion(id + "F80", true);
            extrude(context, id + "F81", {"entities" : qUnion([Q0]), "operationType" : NewBodyOperationType.REMOVE, "oppositeDirection" : true, "depth" : 1020 * mm, "offsetDistance" : 25 * mm});
        }
        {
            var Q0;
            Q0=makeQuery(id+"F49.opExtrude","CAP_FACE",FACE,{"disambiguationData":[OSD([sQuery(id+"F48.wireOp",EDGE,"E109")])],"isStart":false});
            var sketch = newSketch(context, id + "F82", { "sketchPlane" : qUnion([Q0])});
            skCircle(sketch, "E129", {"center": v(-100, 1500) * mm, "radius": 15 * mm});
            skSolve(sketch);
        }
        {
            var Q0;
            Q0 = qSketchRegion(id + "F82", true);
            extrude(context, id + "F83", {"entities" : qUnion([Q0]), "operationType" : NewBodyOperationType.REMOVE, "oppositeDirection" : true, "depth" : 1020 * mm, "offsetDistance" : 25 * mm});
        }
        {
            var Q0;
            Q0=makeQuery(id+"F35.opExtrude","CAP_FACE",FACE,{"disambiguationData":[OSD([sQuery(id+"F33.wireOp",EDGE,"E84")])],"isStart":false});
            var sketch = newSketch(context, id + "F84", { "sketchPlane" : qUnion([Q0])});
            skCircle(sketch, "E130", {"center": v(-600, 1600) * mm, "radius": 15 * mm});
            skSolve(sketch);
        }
        {
            var Q0;
            Q0 = qSketchRegion(id + "F84", true);
            extrude(context, id + "F85", {"entities" : qUnion([Q0]), "operationType" : NewBodyOperationType.REMOVE, "oppositeDirection" : true, "depth" : 200 * mm, "offsetDistance" : 25 * mm});
        }
        {
            var Q0;
            Q0=makeQuery(id+"F59.opExtrude","CAP_FACE",FACE,{"disambiguationData":[OSD([sQuery(id+"F57.wireOp",EDGE,"E116")])],"isStart":true});
            var sketch = newSketch(context, id + "F86", { "sketchPlane" : qUnion([Q0])});
            skCircle(sketch, "E131", {"center": v(-100, 1600) * mm, "radius": 15 * mm});
            skSolve(sketch);
        }
        {
            var Q0;
            Q0 = qSketchRegion(id + "F86", true);
            extrude(context, id + "F87", {"entities" : qUnion([Q0]), "operationType" : NewBodyOperationType.REMOVE, "oppositeDirection" : true, "depth" : 200 * mm, "offsetDistance" : 25 * mm});
        }
        {
            var Q0;
            Q0=makeQuery(id+"F46.opExtrude","CAP_FACE",FACE,{"disambiguationData":[OSD([sQuery(id+"F45.wireOp",EDGE,"E106")])],"isStart":false});
            var sketch = newSketch(context, id + "F88", { "sketchPlane" : qUnion([Q0])});
            skCircle(sketch, "E132", {"center": v(100, 1500) * mm, "radius": 15 * mm});
            skSolve(sketch);
        }
        {
            var Q0;
            Q0 = qSketchRegion(id + "F88", true);
            extrude(context, id + "F89", {"entities" : qUnion([Q0]), "operationType" : NewBodyOperationType.REMOVE, "oppositeDirection" : true, "depth" : 1020 * mm, "offsetDistance" : 25 * mm});
        }
        {
            var Q0;
            Q0=makeQuery(id+"F25.opExtrude","CAP_FACE",FACE,{"disambiguationData":[OSD([sQuery(id+"F24.wireOp",EDGE,"E79")])],"isStart":false});
            var sketch = newSketch(context, id + "F90", { "sketchPlane" : qUnion([Q0])});
            skCircle(sketch, "E133", {"center": v(600, 1500) * mm, "radius": 15 * mm});
            skSolve(sketch);
        }
        {
            var Q0;
            Q0 = qSketchRegion(id + "F90", true);
            extrude(context, id + "F91", {"entities" : qUnion([Q0]), "operationType" : NewBodyOperationType.REMOVE, "oppositeDirection" : true, "depth" : 1020 * mm, "offsetDistance" : 25 * mm});
        }
        {
            var Q0;
            Q0=makeQuery(id+"F46.opExtrude","CAP_FACE",FACE,{"disambiguationData":[OSD([sQuery(id+"F45.wireOp",EDGE,"E107")])],"isStart":false});
            var sketch = newSketch(context, id + "F92", { "sketchPlane" : qUnion([Q0])});
            skCircle(sketch, "E134", {"center": v(100, 950) * mm, "radius": 15 * mm});
            skSolve(sketch);
        }
        {
            var Q0;
            Q0 = qSketchRegion(id + "F92", true);
            extrude(context, id + "F93", {"entities" : qUnion([Q0]), "operationType" : NewBodyOperationType.REMOVE, "oppositeDirection" : true, "depth" : 1020 * mm, "offsetDistance" : 25 * mm});
        }
        {
            var Q0;
            Q0=makeQuery(id+"F25.opExtrude","CAP_FACE",FACE,{"disambiguationData":[OSD([sQuery(id+"F24.wireOp",EDGE,"E80")])],"isStart":false});
            var sketch = newSketch(context, id + "F94", { "sketchPlane" : qUnion([Q0])});
            skCircle(sketch, "E135", {"center": v(600, 950) * mm, "radius": 15 * mm});
            skSolve(sketch);
        }
        {
            var Q0;
            Q0 = qSketchRegion(id + "F94", true);
            extrude(context, id + "F95", {"entities" : qUnion([Q0]), "operationType" : NewBodyOperationType.REMOVE, "oppositeDirection" : true, "depth" : 1020 * mm, "offsetDistance" : 25 * mm});
        }
        {
            var Q0;
            Q0=makeQuery(id+"F46.opExtrude","CAP_FACE",FACE,{"disambiguationData":[OSD([sQuery(id+"F45.wireOp",EDGE,"E108")])],"isStart":false});
            var sketch = newSketch(context, id + "F96", { "sketchPlane" : qUnion([Q0])});
            skCircle(sketch, "E136", {"center": v(100, 400) * mm, "radius": 15 * mm});
            skSolve(sketch);
        }
        {
            var Q0;
            Q0 = qSketchRegion(id + "F96", true);
            extrude(context, id + "F97", {"entities" : qUnion([Q0]), "operationType" : NewBodyOperationType.REMOVE, "oppositeDirection" : true, "depth" : 1020 * mm, "offsetDistance" : 25 * mm});
        }
        {
            var Q0;
            Q0=makeQuery(id+"F25.opExtrude","CAP_FACE",FACE,{"disambiguationData":[OSD([sQuery(id+"F24.wireOp",EDGE,"E81")])],"isStart":false});
            var sketch = newSketch(context, id + "F98", { "sketchPlane" : qUnion([Q0])});
            skCircle(sketch, "E137", {"center": v(600, 400) * mm, "radius": 15 * mm});
            skSolve(sketch);
        }
        {
            var Q0;
            Q0 = qSketchRegion(id + "F98", true);
            extrude(context, id + "F99", {"entities" : qUnion([Q0]), "operationType" : NewBodyOperationType.REMOVE, "oppositeDirection" : true, "depth" : 1020 * mm, "offsetDistance" : 25 * mm});
        }
        {
            var Q0;
            Q0=makeQuery(id+"F15.opExtrude","CAP_FACE",FACE,{"disambiguationData":[OSD([sQuery(id+"F14.wireOp",EDGE,"E57")])],"isStart":false});
            var sketch = newSketch(context, id + "F100", { "sketchPlane" : qUnion([Q0])});
            skCircle(sketch, "E138", {"center": v(600, -35) * mm, "radius": 15 * mm});
            skSolve(sketch);
        }
        {
            var Q0;
            Q0 = qSketchRegion(id + "F100", true);
            extrude(context, id + "F101", {"entities" : qUnion([Q0]), "operationType" : NewBodyOperationType.REMOVE, "oppositeDirection" : true, "depth" : 2300 * mm, "offsetDistance" : 25 * mm});
        }
        {
            var Q0;
            Q0=makeQuery(id+"F15.opExtrude","CAP_FACE",FACE,{"disambiguationData":[OSD([sQuery(id+"F14.wireOp",EDGE,"E56")])],"isStart":false});
            var sketch = newSketch(context, id + "F102", { "sketchPlane" : qUnion([Q0])});
            skCircle(sketch, "E139", {"center": v(100, -35) * mm, "radius": 15 * mm});
            skSolve(sketch);
        }
        {
            var Q0;
            Q0 = qSketchRegion(id + "F102", true);
            extrude(context, id + "F103", {"entities" : qUnion([Q0]), "operationType" : NewBodyOperationType.REMOVE, "oppositeDirection" : true, "depth" : 2300 * mm, "offsetDistance" : 25 * mm});
        }
        {
            var Q0;
            Q0=makeQuery(id+"F4.opExtrude","CAP_FACE",FACE,{"disambiguationData":[OSD([sQuery(id+"F3.wireOp",EDGE,"E14")])],"isStart":true});
            var sketch = newSketch(context, id + "F104", { "sketchPlane" : qUnion([Q0])});
            skCircle(sketch, "E140", {"center": v(-1042.1, 0) * mm, "radius": 15 * mm});
            skSolve(sketch);
        }
        {
            var Q0;
            Q0 = qSketchRegion(id + "F104", true);
            extrude(context, id + "F105", {"entities" : qUnion([Q0]), "operationType" : NewBodyOperationType.REMOVE, "oppositeDirection" : true, "depth" : 700 * mm, "offsetDistance" : 25 * mm});
        }
        {
            var Q0;
            Q0=makeQuery(id+"F4.opExtrude","CAP_FACE",FACE,{"disambiguationData":[OSD([sQuery(id+"F3.wireOp",EDGE,"E15")])],"isStart":true});
            var sketch = newSketch(context, id + "F106", { "sketchPlane" : qUnion([Q0])});
            skCircle(sketch, "E141", {"center": v(1057.9, 0) * mm, "radius": 15 * mm});
            skSolve(sketch);
        }
        {
            var Q0;
            Q0 = qSketchRegion(id + "F106", true);
            extrude(context, id + "F107", {"entities" : qUnion([Q0]), "operationType" : NewBodyOperationType.REMOVE, "oppositeDirection" : true, "depth" : 700 * mm, "offsetDistance" : 25 * mm});
        }
    });
